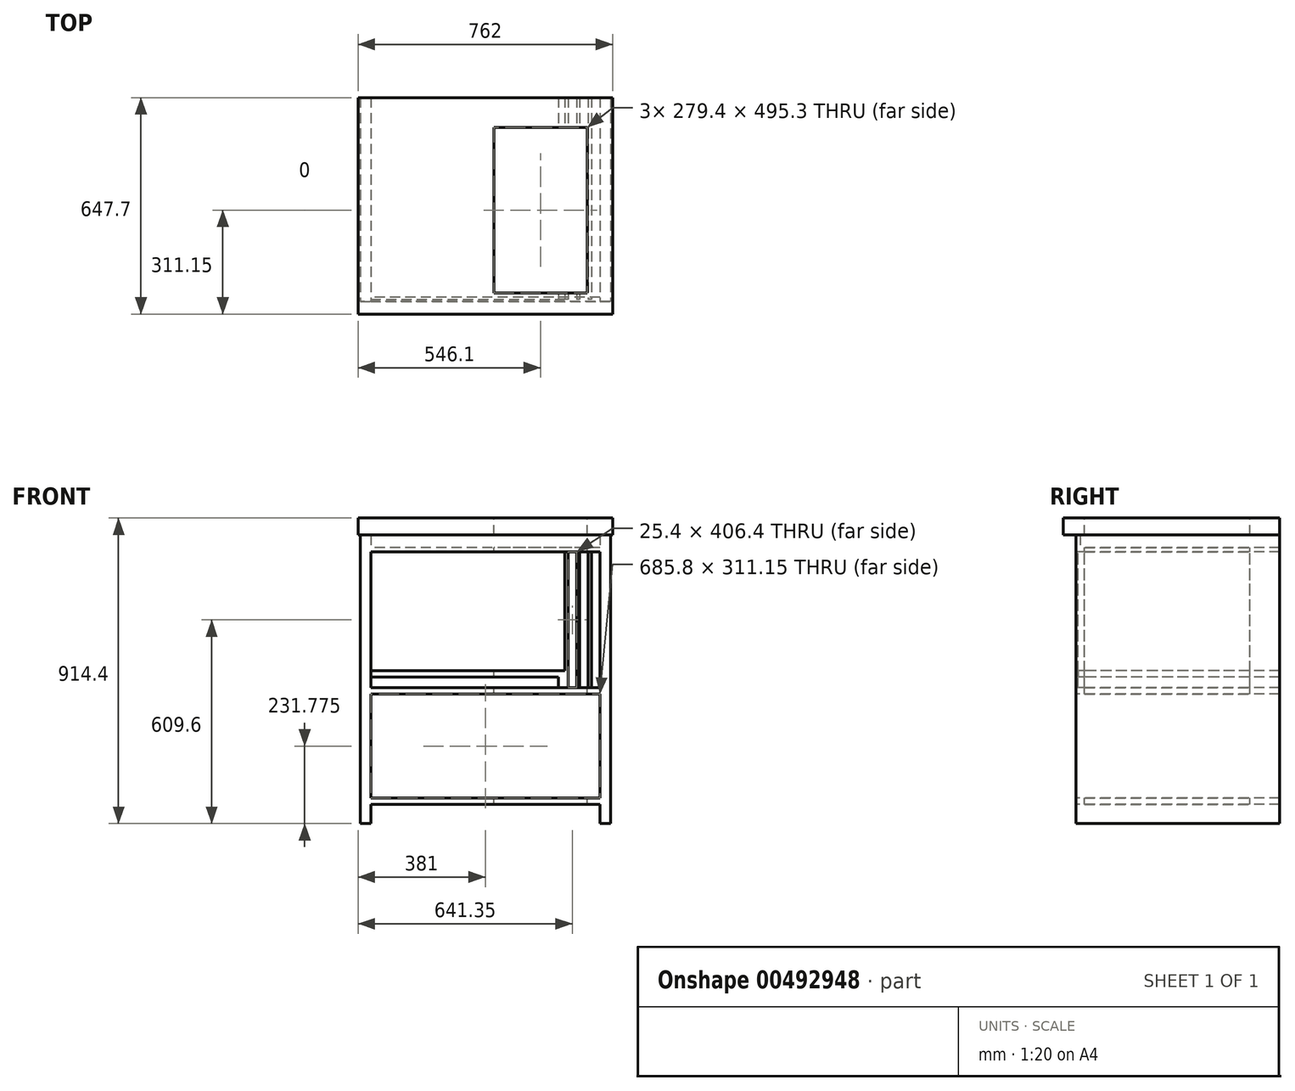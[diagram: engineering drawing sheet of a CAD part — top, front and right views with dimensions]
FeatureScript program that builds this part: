
annotation { "Feature Type Name" : "Feature", "Feature Type Description" : "" }
export const myFeature = defineFeature(function(context is Context, id is Id, definition is map)
    precondition{}
    {
        {
            var Q0;
            Q0=qCreatedBy(makeId("Front.planeOp"),FACE);
            var sketch = newSketch(context, id + "F0", { "sketchPlane" : qUnion([Q0])});
            skLineSegment(sketch, "E0.bottom", {"start": v(-374.65, 457.2) * mm, "end": v(374.65, 457.2) * mm});
            skLineSegment(sketch, "E0.top", {"start": v(-374.65, -457.2) * mm, "end": v(-342.9, -457.2) * mm});
            skLineSegment(sketch, "E0.left", {"start": v(-374.65, 406.4) * mm, "end": v(-374.65, -457.2) * mm});
            skLineSegment(sketch, "E0.right", {"start": v(374.65, 406.4) * mm, "end": v(374.65, -457.2) * mm});
            skPoint(sketch, "E0.middle", {"position": v(0, 0) * mm});
            skLineSegment(sketch, "E1", {"start": v(-342.9, -50.8) * mm, "end": v(342.9, -50.8) * mm});
            skLineSegment(sketch, "E2", {"start": v(-342.9, -69.85) * mm, "end": v(342.9, -69.85) * mm});
            skLineSegment(sketch, "E3", {"start": v(-342.9, -381) * mm, "end": v(342.9, -381) * mm});
            skLineSegment(sketch, "E4", {"start": v(-342.9, -400.05) * mm, "end": v(342.9, -400.05) * mm});
            skLineSegment(sketch, "E5", {"start": v(-374.65, 355.6) * mm, "end": v(374.65, 355.6) * mm});
            skLineSegment(sketch, "E6", {"start": v(-342.9, -457.2) * mm, "end": v(-342.9, 355.6) * mm});
            skLineSegment(sketch, "E7", {"start": v(342.9, -457.2) * mm, "end": v(342.9, 355.6) * mm});
            skLineSegment(sketch, "E8", {"start": v(-342.9, 355.6) * mm, "end": v(-342.9, 406.4) * mm});
            skLineSegment(sketch, "E9", {"start": v(342.9, 355.6) * mm, "end": v(342.9, 406.4) * mm});
            skLineSegment(sketch, "E10", {"start": v(-342.9, 368.3) * mm, "end": v(342.9, 368.3) * mm});
            skLineSegment(sketch, "E11.bottom", {"start": v(238.13, 355.6) * mm, "end": v(247.65, 355.6) * mm});
            skLineSegment(sketch, "E11.top", {"start": v(238.13, -50.8) * mm, "end": v(247.65, -50.8) * mm});
            skLineSegment(sketch, "E11.left", {"start": v(238.13, 355.6) * mm, "end": v(238.13, -50.8) * mm});
            skLineSegment(sketch, "E11.right", {"start": v(247.65, 355.6) * mm, "end": v(247.65, -50.8) * mm});
            skLineSegment(sketch, "E12.bottom", {"start": v(273.05, 355.6) * mm, "end": v(282.58, 355.6) * mm});
            skLineSegment(sketch, "E12.top", {"start": v(273.05, -50.8) * mm, "end": v(282.58, -50.8) * mm});
            skLineSegment(sketch, "E12.left", {"start": v(273.05, 355.6) * mm, "end": v(273.05, -50.8) * mm});
            skLineSegment(sketch, "E12.right", {"start": v(282.58, 355.6) * mm, "end": v(282.58, -50.8) * mm});
            skLineSegment(sketch, "E13.bottom", {"start": v(307.98, 355.6) * mm, "end": v(317.5, 355.6) * mm});
            skLineSegment(sketch, "E13.top", {"start": v(307.98, -50.8) * mm, "end": v(317.5, -50.8) * mm});
            skLineSegment(sketch, "E13.left", {"start": v(307.98, 355.6) * mm, "end": v(307.98, -50.8) * mm});
            skLineSegment(sketch, "E13.right", {"start": v(317.5, 355.6) * mm, "end": v(317.5, -50.8) * mm});
            skLineSegment(sketch, "E14.bottom", {"start": v(238.13, 0) * mm, "end": v(-342.9, 0) * mm});
            skLineSegment(sketch, "E14.top", {"start": v(238.13, -19.05) * mm, "end": v(-342.9, -19.05) * mm});
            skLineSegment(sketch, "E14.left", {"start": v(238.13, 0) * mm, "end": v(238.13, -19.05) * mm});
            skLineSegment(sketch, "E14.right", {"start": v(-342.9, 0) * mm, "end": v(-342.9, -19.05) * mm});
            skLineSegment(sketch, "E15", {"start": v(247.65, 152.4) * mm, "end": v(273.05, 152.4) * mm, "construction": true});
            skLineSegment(sketch, "E16", {"start": v(282.58, 152.4) * mm, "end": v(307.98, 152.4) * mm, "construction": true});
            skLineSegment(sketch, "E17", {"start": v(-381, 457.2) * mm, "end": v(-381, 406.4) * mm});
            skLineSegment(sketch, "E18", {"start": v(381, 406.4) * mm, "end": v(381, 457.2) * mm});
            skLineSegment(sketch, "E19", {"start": v(374.65, 457.2) * mm, "end": v(-374.65, 457.2) * mm});
            skLineSegment(sketch, "E20", {"start": v(0, 457.2) * mm, "end": v(0, 0) * mm, "construction": true});
            skLineSegment(sketch, "E21", {"start": v(381, 406.4) * mm, "end": v(-381, 406.4) * mm});
            skLineSegment(sketch, "E22", {"start": v(-374.65, 457.2) * mm, "end": v(-381, 457.2) * mm});
            skLineSegment(sketch, "E23", {"start": v(374.65, 457.2) * mm, "end": v(381, 457.2) * mm});
            skLineSegment(sketch, "E24.trimOffspring", {"start": v(342.9, -457.2) * mm, "end": v(374.65, -457.2) * mm});
            skLineSegment(sketch, "E25.top", {"start": v(-334.6, 330.2) * mm, "end": v(214.67, 330.2) * mm, "construction": true});
            skLineSegment(sketch, "E25.left", {"start": v(-334.6, 0) * mm, "end": v(-334.6, 330.2) * mm, "construction": true});
            skLineSegment(sketch, "E25.right", {"start": v(214.67, 0) * mm, "end": v(214.67, 330.2) * mm, "construction": true});
            skLineSegment(sketch, "E26", {"start": v(317.5, 152.4) * mm, "end": v(342.9, 152.4) * mm, "construction": true});
            skLineSegment(sketch, "E27", {"start": v(219.08, -19.05) * mm, "end": v(219.08, -50.8) * mm});
            skSolve(sketch);
        }
        {
            var Q0;
            {var subQ0=sQuery(id+"F0.wireOp",EDGE,"E6");var subQ6=sQuery(id+"F0.wireOp",EDGE,"E0.top");var subQ8=makeQuery(id+"F0.imprint","INTERSECT",VERTEX,{"derivedFrom":[subQ6,subQ0]});Q0=makeQuery(id+"F0.imprint","IMPRINT",FACE,{"disambiguationData":[TD([[makeQuery(id+"F0.imprint","IMPRINT",EDGE,{"disambiguationData":[TD([[subQ8,1.0]])],"derivedFrom":subQ6}),1.0]])]});}
            var Q1;
            {var subQ1=sQuery(id+"F0.wireOp",EDGE,"E0.right");var subQ7=sQuery(id+"F0.wireOp",EDGE,"E0.top");var subQ8=makeQuery(id+"F0.imprint","INTERSECT",VERTEX,{"derivedFrom":[subQ7,subQ1]});Q1=makeQuery(id+"F0.imprint","IMPRINT",FACE,{"disambiguationData":[TD([[makeQuery(id+"F0.imprint","IMPRINT",EDGE,{"disambiguationData":[TD([[subQ8,1.0]])],"derivedFrom":subQ7}),1.0]])]});}
            var Q2;
            {var subQ0=sQuery(id+"F0.wireOp",EDGE,"E1");Q2=makeQuery(id+"F0.imprint","IMPRINT",FACE,{"disambiguationData":[TD([[makeQuery(id+"F0.imprint","IMPRINT",EDGE,{"derivedFrom":subQ0}),-1.0]])]});}
            var Q3;
            {var subQ0=sQuery(id+"F0.wireOp",EDGE,"E3");Q3=makeQuery(id+"F0.imprint","IMPRINT",FACE,{"disambiguationData":[TD([[makeQuery(id+"F0.imprint","IMPRINT",EDGE,{"derivedFrom":subQ0}),-1.0]])]});}
            var Q4;
            {var subQ5=sQuery(id+"F0.wireOp",EDGE,"E8");Q4=makeQuery(id+"F0.imprint","IMPRINT",FACE,{"disambiguationData":[TD([[makeQuery(id+"F0.imprint","IMPRINT",EDGE,{"derivedFrom":subQ5}),1.0]])]});}
            var Q5;
            {var subQ5=sQuery(id+"F0.wireOp",EDGE,"E9");Q5=makeQuery(id+"F0.imprint","IMPRINT",FACE,{"disambiguationData":[TD([[makeQuery(id+"F0.imprint","IMPRINT",EDGE,{"derivedFrom":subQ5}),-1.0]])]});}
            var Q6;
            {var subQ5=sQuery(id+"F0.wireOp",EDGE,"E10");Q6=makeQuery(id+"F0.imprint","IMPRINT",FACE,{"disambiguationData":[TD([[makeQuery(id+"F0.imprint","IMPRINT",EDGE,{"derivedFrom":subQ5}),-1.0]])]});}
            var Q7;
            {var subQ0=sQuery(id+"F0.wireOp",EDGE,"E5");var subQ12=makeQuery(id+"F0.imprint","INTERSECT",VERTEX,{"derivedFrom":[subQ0,sQuery(id+"F0.wireOp",EDGE,"E11.left")]});Q7=makeQuery(id+"F0.imprint","IMPRINT",FACE,{"disambiguationData":[TD([[makeQuery(id+"F0.imprint","IMPRINT",EDGE,{"disambiguationData":[TD([[subQ12,1.0]])],"derivedFrom":subQ0}),1.0]])]});}
            var Q8;
            {var subQ8=sQuery(id+"F0.wireOp",EDGE,"E24.trimOffspring");Q8=makeQuery(id+"F0.imprint","IMPRINT",FACE,{"disambiguationData":[TD([[makeQuery(id+"F0.imprint","IMPRINT",EDGE,{"derivedFrom":subQ8}),1.0]])]});}
            extrude(context, id + "F1", {"entities" : qUnion([Q0, Q1, Q2, Q3, Q4, Q5, Q6, Q7, Q8]), "oppositeDirection" : true, "depth" : 647.7 * mm, "offsetDistance" : 25.4 * mm, "hasSecondDirection" : true, "secondDirectionOppositeDirection" : true, "secondDirectionDepth" : 38.1 * mm});
        }
        {
            var Q0;
            {var subQ0=sQuery(id+"F0.wireOp",EDGE,"E11.left");Q0=makeQuery(id+"F0.imprint","IMPRINT",FACE,{"disambiguationData":[TD([[makeQuery(id+"F0.imprint","IMPRINT",EDGE,{"derivedFrom":subQ0}),1.0]])]});}
            var Q1;
            {var subQ4=sQuery(id+"F0.wireOp",EDGE,"E1");var subQ6=sQuery(id+"F0.wireOp",EDGE,"E12.right");var subQ8=makeQuery(id+"F0.imprint","INTERSECT",VERTEX,{"derivedFrom":[subQ4,subQ6]});Q1=makeQuery(id+"F0.imprint","IMPRINT",FACE,{"disambiguationData":[TD([[makeQuery(id+"F0.imprint","IMPRINT",EDGE,{"disambiguationData":[TD([[subQ8,1.0]])],"derivedFrom":subQ4}),1.0]])]});}
            var Q2;
            {var subQ2=sQuery(id+"F0.wireOp",EDGE,"E1");var subQ6=sQuery(id+"F0.wireOp",EDGE,"E13.right");var subQ8=makeQuery(id+"F0.imprint","INTERSECT",VERTEX,{"derivedFrom":[subQ2,subQ6]});Q2=makeQuery(id+"F0.imprint","IMPRINT",FACE,{"disambiguationData":[TD([[makeQuery(id+"F0.imprint","IMPRINT",EDGE,{"disambiguationData":[TD([[subQ8,1.0]])],"derivedFrom":subQ2}),1.0]])]});}
            var Q3;
            {var subQ6=sQuery(id+"F0.wireOp",EDGE,"IyCdlQwl-Seli-yWye-hXe8-IG1xyl1ce54z.right");Q3=makeQuery(id+"F0.imprint","IMPRINT",FACE,{"disambiguationData":[TD([[makeQuery(id+"F0.imprint","IMPRINT",EDGE,{"derivedFrom":subQ6}),-1.0]])]});}
            var Q4;
            {var subQ0=sQuery(id+"F0.wireOp",EDGE,"51DnjMUQ-nPbv-QU9U-Dl2P-IHuoqzXLhzBb.left");Q4=makeQuery(id+"F0.imprint","IMPRINT",FACE,{"disambiguationData":[TD([[makeQuery(id+"F0.imprint","IMPRINT",EDGE,{"derivedFrom":subQ0}),1.0]])]});}
            var Q5;
            {var subQ0=sQuery(id+"F0.wireOp",EDGE,"E14.bottom");Q5=makeQuery(id+"F0.imprint","IMPRINT",FACE,{"disambiguationData":[TD([[makeQuery(id+"F0.imprint","IMPRINT",EDGE,{"derivedFrom":subQ0}),1.0]])]});}
            var Q6;
            {var subQ0=sQuery(id+"F0.wireOp",EDGE,"E27");Q6=makeQuery(id+"F0.imprint","IMPRINT",FACE,{"disambiguationData":[TD([[makeQuery(id+"F0.imprint","IMPRINT",EDGE,{"derivedFrom":subQ0}),1.0]])]});}
            var Q7;
            Q7=makeQuery(id+"F1.opExtrude","CAP_FACE",FACE,{"disambiguationData":[OSD([sQuery(id+"F0.wireOp",EDGE,"E0.top"),sQuery(id+"F0.wireOp",EDGE,"E0.left"),sQuery(id+"F0.wireOp",EDGE,"E0.right"),sQuery(id+"F0.wireOp",EDGE,"UFNqajwX-M1Zc-nUOi-uk6F-VzglLgCA9skw"),sQuery(id+"F0.wireOp",EDGE,"E1"),sQuery(id+"F0.wireOp",EDGE,"E2"),sQuery(id+"F0.wireOp",EDGE,"E3"),sQuery(id+"F0.wireOp",EDGE,"E4"),sQuery(id+"F0.wireOp",EDGE,"E5"),sQuery(id+"F0.wireOp",EDGE,"E6"),sQuery(id+"F0.wireOp",EDGE,"E7"),sQuery(id+"F0.wireOp",EDGE,"E8"),sQuery(id+"F0.wireOp",EDGE,"E9"),sQuery(id+"F0.wireOp",EDGE,"E10")])],"isStart":false});
            var Q8;
            Q8=makeQuery(id+"F1.opExtrude","CAP_FACE",FACE,{"disambiguationData":[OSD([sQuery(id+"F0.wireOp",EDGE,"E0.top"),sQuery(id+"F0.wireOp",EDGE,"E0.left"),sQuery(id+"F0.wireOp",EDGE,"E0.right"),sQuery(id+"F0.wireOp",EDGE,"UFNqajwX-M1Zc-nUOi-uk6F-VzglLgCA9skw"),sQuery(id+"F0.wireOp",EDGE,"E1"),sQuery(id+"F0.wireOp",EDGE,"E2"),sQuery(id+"F0.wireOp",EDGE,"E3"),sQuery(id+"F0.wireOp",EDGE,"E4"),sQuery(id+"F0.wireOp",EDGE,"E5"),sQuery(id+"F0.wireOp",EDGE,"E6"),sQuery(id+"F0.wireOp",EDGE,"E7"),sQuery(id+"F0.wireOp",EDGE,"E8"),sQuery(id+"F0.wireOp",EDGE,"E9"),sQuery(id+"F0.wireOp",EDGE,"E10")])],"isStart":true});
            extrude(context, id + "F2", {"entities" : qUnion([Q0, Q1, Q2, Q3, Q4, Q5, Q6]), "operationType" : NewBodyOperationType.ADD, "endBound" : BoundingType.UP_TO_SURFACE, "oppositeDirection" : true, "depth" : 25.4 * mm, "endBoundEntityFace" : qUnion([Q7]), "offsetDistance" : 25.4 * mm, "hasSecondDirection" : true, "secondDirectionBound" : BoundingType.UP_TO_SURFACE, "secondDirectionOppositeDirection" : true, "secondDirectionDepth" : 25.4 * mm, "secondDirectionBoundEntityFace" : qUnion([Q8]), "hasSecondDirectionOffset" : true, "secondDirectionOffsetDistance" : 6.35 * mm, "secondDirectionOffsetOppositeDirection" : true});
        }
        {
            var Q0;
            {var subQ1=sQuery(id+"F0.wireOp",EDGE,"E0.bottom");Q0=makeQuery(id+"F0.imprint","IMPRINT",FACE,{"disambiguationData":[TD([[makeQuery(id+"F0.imprint","IMPRINT",EDGE,{"derivedFrom":subQ1}),-1.0]])]});}
            var Q1;
            Q1=makeQuery(id+"F1.opExtrude","CAP_FACE",FACE,{"disambiguationData":[OSD([sQuery(id+"F0.wireOp",EDGE,"E0.top"),sQuery(id+"F0.wireOp",EDGE,"E0.left"),sQuery(id+"F0.wireOp",EDGE,"E0.right"),sQuery(id+"F0.wireOp",EDGE,"UFNqajwX-M1Zc-nUOi-uk6F-VzglLgCA9skw"),sQuery(id+"F0.wireOp",EDGE,"E1"),sQuery(id+"F0.wireOp",EDGE,"E2"),sQuery(id+"F0.wireOp",EDGE,"E3"),sQuery(id+"F0.wireOp",EDGE,"E4"),sQuery(id+"F0.wireOp",EDGE,"E6"),sQuery(id+"F0.wireOp",EDGE,"E7"),sQuery(id+"F0.wireOp",EDGE,"E8"),sQuery(id+"F0.wireOp",EDGE,"E9")])],"isStart":false});
            extrude(context, id + "F3", {"entities" : qUnion([Q0]), "endBound" : BoundingType.UP_TO_SURFACE, "oppositeDirection" : true, "depth" : 25.4 * mm, "endBoundEntityFace" : qUnion([Q1]), "offsetDistance" : 25.4 * mm});
        }
        {
            var Q0;
            Q0=makeQuery(id+"F3.opExtrude","SWEPT_FACE",FACE,{"disambiguationData":[OSD([sQuery(id+"F0.wireOp",EDGE,"E0.bottom")])]});
            var sketch = newSketch(context, id + "F4", { "sketchPlane" : qUnion([Q0])});
            skLineSegment(sketch, "E28.bottom", {"start": v(25.4, 558.8) * mm, "end": v(304.8, 558.8) * mm});
            skLineSegment(sketch, "E28.top", {"start": v(25.4, 63.5) * mm, "end": v(304.8, 63.5) * mm});
            skLineSegment(sketch, "E28.left", {"start": v(25.4, 558.8) * mm, "end": v(25.4, 63.5) * mm});
            skLineSegment(sketch, "E28.right", {"start": v(304.8, 558.8) * mm, "end": v(304.8, 63.5) * mm});
            skPoint(sketch, "E28.middle", {"position": v(165.1, 311.15) * mm});
            skSolve(sketch);
        }
        {
            var Q0;
            Q0 = qSketchRegion(id + "F4", true);
            extrude(context, id + "F5", {"entities" : qUnion([Q0]), "operationType" : NewBodyOperationType.REMOVE, "endBound" : BoundingType.THROUGH_ALL, "oppositeDirection" : true, "depth" : 25.4 * mm, "offsetDistance" : 25.4 * mm});
        }
        {
            var Q0;
            {var subQ0=sQuery(id+"F0.wireOp",EDGE,"E10");var subQ1=sQuery(id+"F0.wireOp",EDGE,"E8");var subQ2=makeQuery(id+"F0.imprint","INTERSECT",VERTEX,{"derivedFrom":[subQ1,subQ0]});Q0=makeQuery(id+"F0.imprint","IMPRINT",FACE,{"disambiguationData":[TD([[makeQuery(id+"F0.imprint","IMPRINT",EDGE,{"disambiguationData":[TD([[subQ2,-1.0]])],"derivedFrom":subQ1}),-1.0]])]});}
            var Q1;
            {var subQ0=sQuery(id+"F0.wireOp",EDGE,"E10");var subQ1=sQuery(id+"F0.wireOp",EDGE,"E9");var subQ2=makeQuery(id+"F0.imprint","INTERSECT",VERTEX,{"derivedFrom":[subQ1,subQ0]});Q1=makeQuery(id+"F0.imprint","IMPRINT",FACE,{"disambiguationData":[TD([[makeQuery(id+"F0.imprint","IMPRINT",EDGE,{"disambiguationData":[TD([[subQ2,-1.0]])],"derivedFrom":subQ1}),1.0]])]});}
            var Q2;
            Q2=makeQuery(id+"F1.opExtrude","CAP_FACE",FACE,{"disambiguationData":[OSD([sQuery(id+"F0.wireOp",EDGE,"E0.top"),sQuery(id+"F0.wireOp",EDGE,"E0.left"),sQuery(id+"F0.wireOp",EDGE,"E0.right"),sQuery(id+"F0.wireOp",EDGE,"E1"),sQuery(id+"F0.wireOp",EDGE,"E2"),sQuery(id+"F0.wireOp",EDGE,"E3"),sQuery(id+"F0.wireOp",EDGE,"E4"),sQuery(id+"F0.wireOp",EDGE,"E5"),sQuery(id+"F0.wireOp",EDGE,"E6"),sQuery(id+"F0.wireOp",EDGE,"E7"),sQuery(id+"F0.wireOp",EDGE,"E8"),sQuery(id+"F0.wireOp",EDGE,"E9"),sQuery(id+"F0.wireOp",EDGE,"E10"),sQuery(id+"F0.wireOp",EDGE,"E11.left"),sQuery(id+"F0.wireOp",EDGE,"E11.right"),sQuery(id+"F0.wireOp",EDGE,"E12.left"),sQuery(id+"F0.wireOp",EDGE,"E12.right"),sQuery(id+"F0.wireOp",EDGE,"E13.left"),sQuery(id+"F0.wireOp",EDGE,"E13.right"),sQuery(id+"F0.wireOp",EDGE,"E14.bottom"),sQuery(id+"F0.wireOp",EDGE,"E14.top"),sQuery(id+"F0.wireOp",EDGE,"E21")])],"isStart":true});
            var Q3;
            Q3=makeQuery(id+"F1.opExtrude","CAP_FACE",FACE,{"disambiguationData":[OSD([sQuery(id+"F0.wireOp",EDGE,"E0.top"),sQuery(id+"F0.wireOp",EDGE,"E0.left"),sQuery(id+"F0.wireOp",EDGE,"E0.right"),sQuery(id+"F0.wireOp",EDGE,"E1"),sQuery(id+"F0.wireOp",EDGE,"E2"),sQuery(id+"F0.wireOp",EDGE,"E3"),sQuery(id+"F0.wireOp",EDGE,"E4"),sQuery(id+"F0.wireOp",EDGE,"E5"),sQuery(id+"F0.wireOp",EDGE,"E6"),sQuery(id+"F0.wireOp",EDGE,"E7"),sQuery(id+"F0.wireOp",EDGE,"E8"),sQuery(id+"F0.wireOp",EDGE,"E9"),sQuery(id+"F0.wireOp",EDGE,"E10"),sQuery(id+"F0.wireOp",EDGE,"E11.left"),sQuery(id+"F0.wireOp",EDGE,"E11.right"),sQuery(id+"F0.wireOp",EDGE,"E12.left"),sQuery(id+"F0.wireOp",EDGE,"E12.right"),sQuery(id+"F0.wireOp",EDGE,"E13.left"),sQuery(id+"F0.wireOp",EDGE,"E13.right"),sQuery(id+"F0.wireOp",EDGE,"E14.bottom"),sQuery(id+"F0.wireOp",EDGE,"E14.top"),sQuery(id+"F0.wireOp",EDGE,"E21")])],"isStart":true});
            extrude(context, id + "F6", {"entities" : qUnion([Q0, Q1]), "operationType" : NewBodyOperationType.ADD, "endBound" : BoundingType.UP_TO_SURFACE, "oppositeDirection" : true, "depth" : 25.4 * mm, "endBoundEntityFace" : qUnion([Q2]), "hasOffset" : true, "offsetDistance" : 12.7 * mm, "offsetOppositeDirection" : true, "hasSecondDirection" : true, "secondDirectionBound" : BoundingType.UP_TO_SURFACE, "secondDirectionOppositeDirection" : true, "secondDirectionDepth" : 25.4 * mm, "secondDirectionBoundEntityFace" : qUnion([Q3])});
        }
    });
